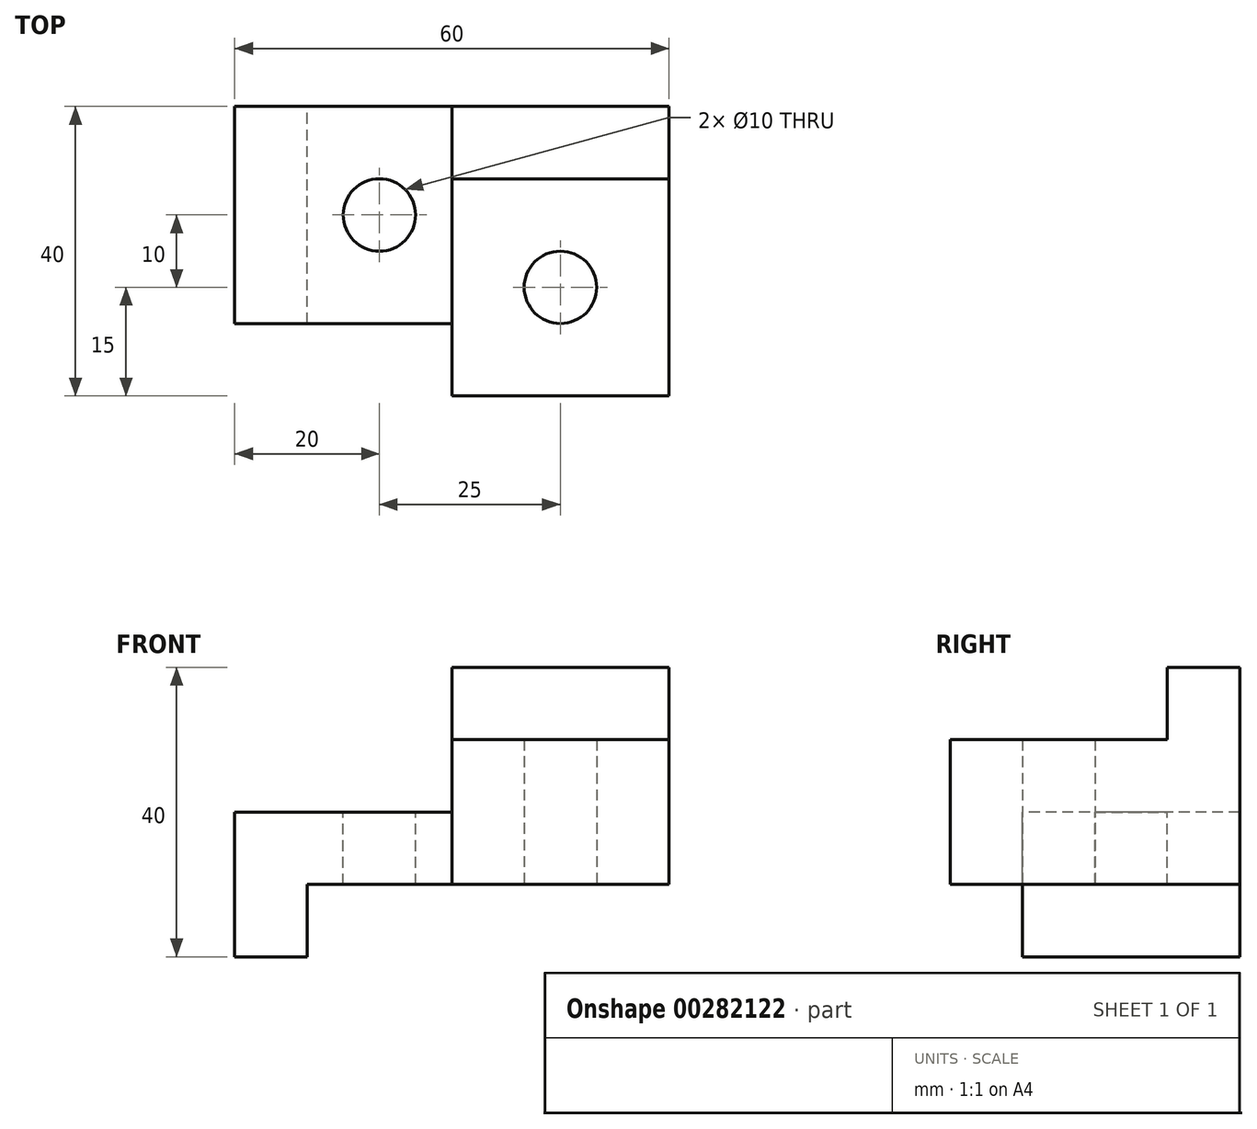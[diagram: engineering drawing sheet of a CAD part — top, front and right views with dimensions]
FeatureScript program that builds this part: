
annotation { "Feature Type Name" : "Feature", "Feature Type Description" : "" }
export const myFeature = defineFeature(function(context is Context, id is Id, definition is map)
    precondition{}
    {
        {
            var Q0;
            Q0=qCreatedBy(makeId("Top.planeOp"),FACE);
            var sketch = newSketch(context, id + "F0", { "sketchPlane" : qUnion([Q0])});
            skLineSegment(sketch, "E0", {"start": v(30, 0) * mm, "end": v(30, 40) * mm});
            skLineSegment(sketch, "E1", {"start": v(30, 40) * mm, "end": v(0, 40) * mm});
            skLineSegment(sketch, "E2", {"start": v(0, 40) * mm, "end": v(0, 0) * mm});
            skLineSegment(sketch, "E3", {"start": v(0, 0) * mm, "end": v(30, 0) * mm});
            skCircle(sketch, "E4", {"center": v(15, 15) * mm, "radius": 5 * mm});
            skSolve(sketch);
        }
        {
            var Q0;
            Q0 = qSketchRegion(id + "F0", true);
            extrude(context, id + "F1", {"entities" : qUnion([Q0]), "depth" : 20 * mm});
        }
        {
            var Q0;
            Q0=makeQuery(id+"F1.opExtrude","CAP_FACE",FACE,{"disambiguationData":[OSD([sQuery(id+"F0.wireOp",EDGE,"E0"),sQuery(id+"F0.wireOp",EDGE,"E1"),sQuery(id+"F0.wireOp",EDGE,"E2"),sQuery(id+"F0.wireOp",EDGE,"E3"),sQuery(id+"F0.wireOp",EDGE,"E4")])],"isStart":false});
            var sketch = newSketch(context, id + "F2", { "sketchPlane" : qUnion([Q0])});
            skLineSegment(sketch, "E5", {"start": v(30, 40) * mm, "end": v(30, 30) * mm});
            skLineSegment(sketch, "E6", {"start": v(30, 30) * mm, "end": v(0, 30) * mm});
            skLineSegment(sketch, "E7", {"start": v(0, 30) * mm, "end": v(0, 40) * mm});
            skLineSegment(sketch, "E8", {"start": v(0, 40) * mm, "end": v(30, 40) * mm});
            skSolve(sketch);
        }
        {
            var Q0;
            Q0 = qSketchRegion(id + "F2", true);
            extrude(context, id + "F3", {"entities" : qUnion([Q0]), "operationType" : NewBodyOperationType.ADD, "depth" : 10 * mm});
        }
        {
            var Q0;
            Q0=makeQuery(id+"F3.boolean.opBoolean","MERGE",FACE,{"derivedFrom":[makeQuery(id+"F1.opExtrude","SWEPT_FACE",FACE,{"disambiguationData":[OSD([sQuery(id+"F0.wireOp",EDGE,"E2")])]}),makeQuery(id+"F3.opExtrude","SWEPT_FACE",FACE,{"disambiguationData":[OSD([sQuery(id+"F2.wireOp",EDGE,"E7")])]})]});
            var sketch = newSketch(context, id + "F4", { "sketchPlane" : qUnion([Q0])});
            skLineSegment(sketch, "E9", {"start": v(-40, 10) * mm, "end": v(-10, 10) * mm});
            skLineSegment(sketch, "E10", {"start": v(-40, 10) * mm, "end": v(-40, 0) * mm});
            skLineSegment(sketch, "E11", {"start": v(-40, 0) * mm, "end": v(-10, 0) * mm});
            skLineSegment(sketch, "E12", {"start": v(-10, 0) * mm, "end": v(-10, 10) * mm});
            skSolve(sketch);
        }
        {
            var Q0;
            Q0=makeQuery(id+"F4.imprint","IMPRINT",FACE,{"disambiguationData":[TD([[makeQuery(id+"F4.imprint","IMPRINT",EDGE,{"derivedFrom":sQuery(id+"F4.wireOp",EDGE,"E9")}),-1.0]])]});
            extrude(context, id + "F5", {"entities" : qUnion([Q0]), "operationType" : NewBodyOperationType.ADD, "depth" : 30 * mm});
        }
        {
            var Q0;
            Q0=makeQuery(id+"F5.opExtrude","SWEPT_FACE",FACE,{"disambiguationData":[OSD([sQuery(id+"F4.wireOp",EDGE,"E9")])]});
            var sketch = newSketch(context, id + "F6", { "sketchPlane" : qUnion([Q0])});
            skCircle(sketch, "E13", {"center": v(-10, 25) * mm, "radius": 5 * mm});
            skSolve(sketch);
        }
        {
            var Q0;
            Q0 = qSketchRegion(id + "F6", true);
            extrude(context, id + "F7", {"entities" : qUnion([Q0]), "operationType" : NewBodyOperationType.REMOVE, "oppositeDirection" : true, "depth" : 25 * mm});
        }
        {
            var Q0;
            Q0=makeQuery(id+"F5.boolean.opBoolean","MERGE",FACE,{"derivedFrom":[makeQuery(id+"F1.opExtrude","CAP_FACE",FACE,{"disambiguationData":[OSD([sQuery(id+"F0.wireOp",EDGE,"E0"),sQuery(id+"F0.wireOp",EDGE,"E1"),sQuery(id+"F0.wireOp",EDGE,"E2"),sQuery(id+"F0.wireOp",EDGE,"E3"),sQuery(id+"F0.wireOp",EDGE,"E4")])],"isStart":true}),makeQuery(id+"F5.opExtrude","SWEPT_FACE",FACE,{"disambiguationData":[OSD([sQuery(id+"F4.wireOp",EDGE,"E11")])]})]});
            var sketch = newSketch(context, id + "F8", { "sketchPlane" : qUnion([Q0])});
            skLineSegment(sketch, "E14", {"start": v(-30, -10) * mm, "end": v(-20, -10) * mm});
            skLineSegment(sketch, "E15", {"start": v(-20, -10) * mm, "end": v(-20, -40) * mm});
            skLineSegment(sketch, "E16", {"start": v(-30, -10) * mm, "end": v(-30, -40) * mm});
            skLineSegment(sketch, "E17", {"start": v(-30, -40) * mm, "end": v(-20, -40) * mm});
            skSolve(sketch);
        }
        {
            var Q0;
            Q0 = qSketchRegion(id + "F8", true);
            extrude(context, id + "F9", {"entities" : qUnion([Q0]), "operationType" : NewBodyOperationType.ADD, "depth" : 10 * mm});
        }
    });
